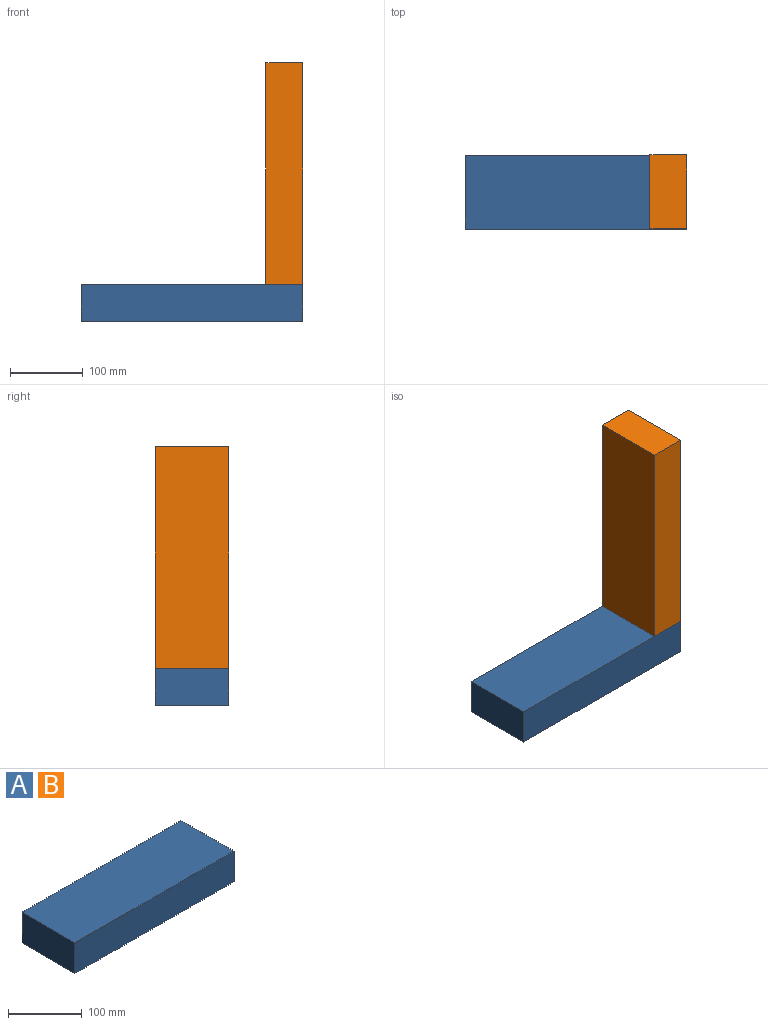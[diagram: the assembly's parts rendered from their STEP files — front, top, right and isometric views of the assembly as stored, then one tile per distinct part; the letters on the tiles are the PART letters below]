
ASSEMBLY  parts=2 mates=1
PART A: 6 faces, bbox 304.8x101.6x50.8 mm
  f0: plane 304.8x50.8mm, normal (0,1,0), area 15483.8mm2, adj f1,f3,f4,f5
  f1: plane 304.8x101.6mm, normal (0,0,1), area 30967.7mm2, adj f0,f2,f4,f5
  f2: plane 304.8x50.8mm, normal (0,-1,0), area 15483.8mm2, adj f1,f3,f4,f5
  f3: plane 304.8x101.6mm, normal (0,0,-1), area 30967.7mm2, adj f0,f2,f4,f5
  f4: plane 101.6x50.8mm, normal (1,0,0), area 5161.3mm2, adj f0,f1,f2,f3
  f5: plane 101.6x50.8mm, normal (-1,0,0), area 5161.3mm2, adj f0,f1,f2,f3
PART B: same geometry as A
PLACE A t=(196,53.29,-21.35)mm
PLACE B rot(axis=(0,1,0),90deg) t=(323,53.29,156.45)mm
MATE fastened B.f1 <-> A.f4  axis (1,0,0) through (348.4,53.29,4.05)mm
